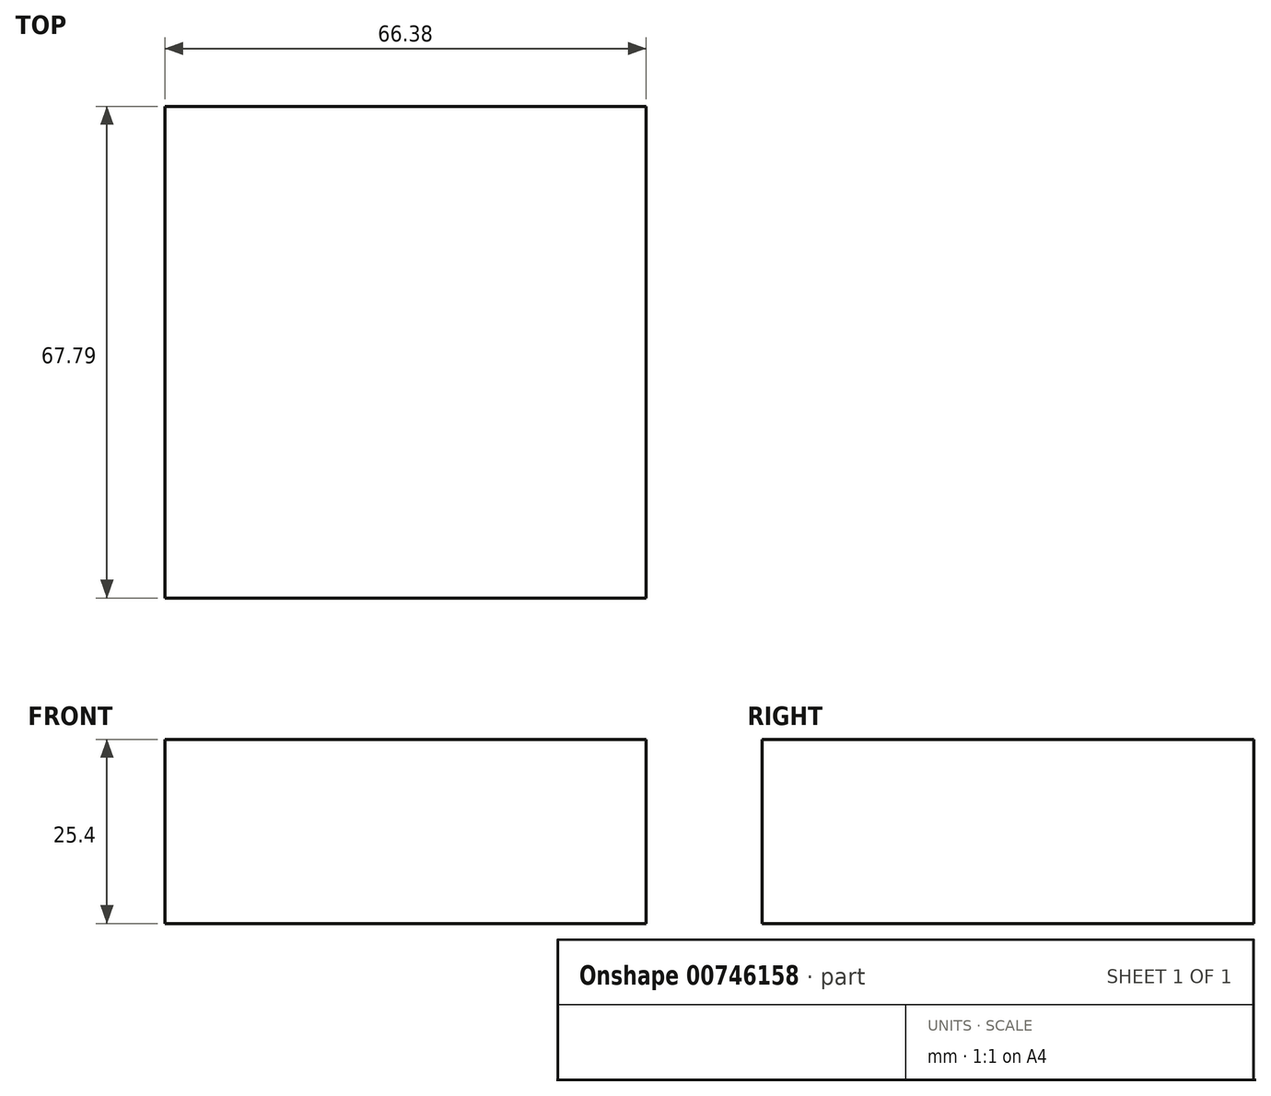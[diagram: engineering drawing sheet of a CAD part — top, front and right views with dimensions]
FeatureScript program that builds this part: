
annotation { "Feature Type Name" : "Feature", "Feature Type Description" : "" }
export const myFeature = defineFeature(function(context is Context, id is Id, definition is map)
    precondition{}
    {
        {
            var Q0;
            Q0=qCreatedBy(makeId("Top.planeOp"),FACE);
            var sketch = newSketch(context, id + "F0", { "sketchPlane" : qUnion([Q0])});
            skLineSegment(sketch, "E0.bottom", {"start": v(0, 0) * mm, "end": v(66.38, 0) * mm});
            skLineSegment(sketch, "E0.top", {"start": v(0, -67.8) * mm, "end": v(66.38, -67.8) * mm});
            skLineSegment(sketch, "E0.left", {"start": v(0, 0) * mm, "end": v(0, -67.8) * mm});
            skLineSegment(sketch, "E0.right", {"start": v(66.38, 0) * mm, "end": v(66.38, -67.8) * mm});
            skSolve(sketch);
        }
        {
            var Q0;
            Q0=makeQuery(id+"F0.imprint","IMPRINT",FACE,{"disambiguationData":[TD([[makeQuery(id+"F0.imprint","IMPRINT",EDGE,{"derivedFrom":sQuery(id+"F0.wireOp",EDGE,"E0.bottom")}),-1.0]])]});
            extrude(context, id + "F1", {"entities" : qUnion([Q0]), "depth" : 25.4 * mm, "offsetDistance" : 25.4 * mm});
        }
    });
